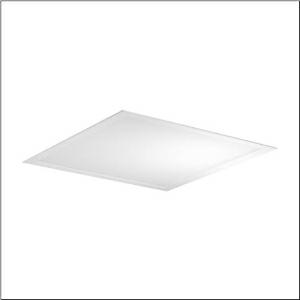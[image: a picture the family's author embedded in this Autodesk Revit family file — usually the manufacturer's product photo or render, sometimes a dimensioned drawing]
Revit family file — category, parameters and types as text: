
# Revit family: apollon_21_square_51mq11wd2454
name_source: partatom
category: Lighting Fixtures
units: mm (PartAtom-declared; Revit-internal decimal feet)

## family parameters
Cut with Voids When Loaded = No
Host = Face
Light Source = No
Part Type = Normal
Room Calculation Point = No
Round Connector Dimension = Use Diameter
Shared = No

## types (1)
- Apollon 21 square (1 x LED, 4200 lm, 24.7 W, 4000K)
    Apparent Load = 25 VA
    CIE Flux Codes = 60 87 97 100 100
    Color Rendering = 80
    Color Temperature = 4000K
    Default Elevation = 1800 mm
    Description = Apollon 21 square, office luminaire, primary optical cover: micro prismatic cover, of PMMA, CAT 2 (L<= 3000cd/m²), light emission: direct distribution, primary light characteristic: symmetric, installation type: lay-in mounting, LED, rated luminous flux: 4.200lm, luminous efficacy: 170lm/W, light colour: 840, colour temperature: 4000K, control gear: DALI 2, Multilumen, with terminal, 5-pole, mains connection: 220..240V, AC/DC, 0/50..60Hz, rated input power: 24.7W, housing, of aluminium, coated, traffic white (RAL 9016), module: M625, length: 620mm, width: 620mm, height: 55mm, recess depth: 180mm, housing upper side, of sheet steel, galvanised, protection rating (complete): IP20, protection rating (lamp compartment, on room side): IP54, insulation class (complete): insulation class II (safety insulation), certification: CE, ENEC, impact resistance: IK03, permissible operating ambient temperature: -20..+45°C, permissible storage temperature: -40..+80°C, standard: EN 60598-2-22, packaging unit: 1 piece
    Height = 0 mm  [stored 0 ft]
    Lamp = 1 x LED
    Lamp Light Flux = 4200 lm
    Lamp Power = 24.7 W
    Lamp count = 1
    Length = 620 mm
    Luminous efficacy = 170 lm/W
    Manufacturer = Siteco
    ModVariant = No
    Model = 51MQ11WD2454
    Mounting Place = Ceiling
    Mounting Type = Recessed
    Number of Poles = 1
    OnlyDefault = Yes
    Power Factor = 1
    Product Name = Apollon 21 square
    Product group = office luminaire | ceiling recessed
    ProductGroupID = 401
    Protection Class = Protection class II
    Protection Degree = IP 20
    RLX_Detail_Level = 1
    RLX_Emergency_Light_Flux = 0 lm
    RLX_Emergency_Type = 0
    RLX_Emergency_Type_DB = No
    RlxData = <blob elided: 13017 chars, md5=d06d9f0a>
    Socket = socket
    Standby Power = 0 W
    System Light Flux = 4200 lm
    System Power = 25 W
    Type Comments = Product without accessories
    Type Image = l_1291054.jpg
    URL = http://relux.com
    VarID = ---
    Voltage = 0 V
    Weight = 0.00 kg
    Width = 620 mm

note: [stored X ft] marks values corroborated as IEEE doubles in the binary element streams (Revit-internal decimal feet)

## geometry (parser evidence)
native form markers: Sweep x11
no freeform markers — native parametric forms only
